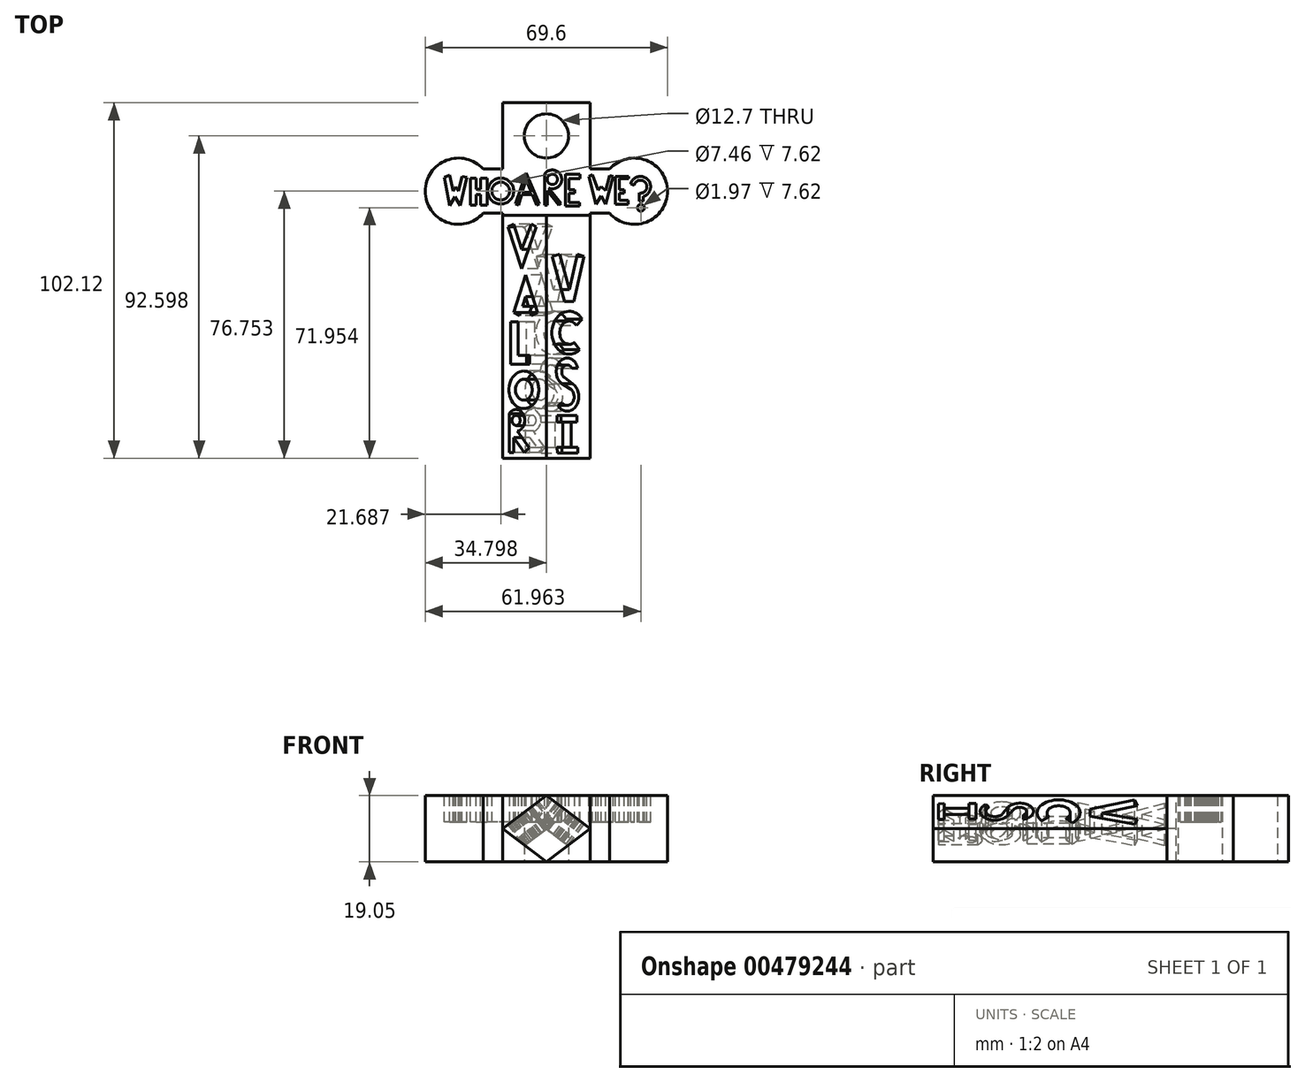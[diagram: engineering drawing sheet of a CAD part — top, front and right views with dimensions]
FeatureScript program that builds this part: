
annotation { "Feature Type Name" : "Feature", "Feature Type Description" : "" }
export const myFeature = defineFeature(function(context is Context, id is Id, definition is map)
    precondition{}
    {
        {
            var Q0;
            Q0=qCreatedBy(makeId("Top.planeOp"),FACE);
            var sketch = newSketch(context, id + "F0", { "sketchPlane" : qUnion([Q0])});
            skLineSegment(sketch, "E0", {"start": v(-32.4, 40.01) * mm, "end": v(-7.25, 40.01) * mm});
            skLineSegment(sketch, "E1", {"start": v(-32.4, 40.01) * mm, "end": v(-32.4, 20.96) * mm});
            skLineSegment(sketch, "E2", {"start": v(-7.25, 40.01) * mm, "end": v(-7.25, 20.96) * mm});
            skLineSegment(sketch, "E3", {"start": v(-7.25, 20.96) * mm, "end": v(5.45, 20.96) * mm});
            skLineSegment(sketch, "E4", {"start": v(-32.4, 20.96) * mm, "end": v(-45.1, 20.96) * mm});
            skLineSegment(sketch, "E5", {"start": v(-45.1, 8.26) * mm, "end": v(5.45, 8.26) * mm});
            skLineSegment(sketch, "E6", {"start": v(-32.4, 8.26) * mm, "end": v(-32.4, -45.49) * mm});
            skLineSegment(sketch, "E7", {"start": v(-7.25, 8.26) * mm, "end": v(-7.25, -45.49) * mm});
            skLineSegment(sketch, "E8", {"start": v(-19.82, 8.26) * mm, "end": v(-19.82, -62.1) * mm});
            skPoint(sketch, "E9.orphan", {"position": v(-7.25, -62.1) * mm});
            skPoint(sketch, "E10.orphan", {"position": v(-32.4, -62.1) * mm});
            skLineSegment(sketch, "E11", {"start": v(-32.4, 20.96) * mm, "end": v(-7.25, 20.96) * mm});
            skCircle(sketch, "E12", {"center": v(-19.82, 30.49) * mm, "radius": 6.35 * mm});
            skPoint(sketch, "E12.centerSnap0", {"position": v(-32.4, 30.49) * mm});
            skPoint(sketch, "E12.centerSnap1", {"position": v(-19.82, 40.01) * mm});
            skLineSegment(sketch, "E13", {"start": v(-7.25, -45.49) * mm, "end": v(-7.25, -62.1) * mm});
            skLineSegment(sketch, "E14", {"start": v(-32.4, -62.1) * mm, "end": v(-32.4, -45.49) * mm});
            skLineSegment(sketch, "E15", {"start": v(-7.25, -62.1) * mm, "end": v(-32.4, -62.1) * mm});
            skLineSegment(sketch, "E16", {"start": v(-19.82, 8.26) * mm, "end": v(-19.82, 20.96) * mm});
            skPoint(sketch, "E17.center.orphan", {"position": v(5.45, 14.61) * mm});
            skPoint(sketch, "E18.center.orphan", {"position": v(-45.1, 14.61) * mm});
            skArc(sketch, "E19", {"start": v(-38, 20.96) * mm, "mid": v(-54.62, 14.61) * mm, "end": v(-38, 8.26) * mm});
            skArc(sketch, "E20", {"start": v(-1.65, 8.26) * mm, "mid": v(14.98, 14.61) * mm, "end": v(-1.65, 20.96) * mm});
            skLineSegment(sketch, "E21", {"start": v(-45.1, 20.96) * mm, "end": v(-45.1, 8.26) * mm});
            skLineSegment(sketch, "E22", {"start": v(5.45, 20.96) * mm, "end": v(5.45, 8.26) * mm});
            skSolve(sketch);
        }
        {
            var Q0;
            Q0=makeQuery(id+"F0.imprint","IMPRINT",FACE,{"disambiguationData":[TD([[makeQuery(id+"F0.imprint","IMPRINT",EDGE,{"derivedFrom":sQuery(id+"F0.wireOp",EDGE,"E0")}),-1.0]])]});
            var Q1;
            {var subQ9=sQuery(id+"F0.wireOp",EDGE,"E16");Q1=makeQuery(id+"F0.imprint","IMPRINT",FACE,{"disambiguationData":[TD([[makeQuery(id+"F0.imprint","IMPRINT",EDGE,{"derivedFrom":subQ9}),1.0]])]});}
            var Q2;
            {var subQ4=sQuery(id+"F0.wireOp",EDGE,"E16");Q2=makeQuery(id+"F0.imprint","IMPRINT",FACE,{"disambiguationData":[TD([[makeQuery(id+"F0.imprint","IMPRINT",EDGE,{"derivedFrom":subQ4}),-1.0]])]});}
            var Q3;
            {var subQ2=sQuery(id+"F0.wireOp",EDGE,"E20");Q3=makeQuery(id+"F0.imprint","IMPRINT",FACE,{"disambiguationData":[TD([[makeQuery(id+"F0.imprint","IMPRINT",EDGE,{"derivedFrom":subQ2}),1.0]])]});}
            var Q4;
            {var subQ2=sQuery(id+"F0.wireOp",EDGE,"E19");Q4=makeQuery(id+"F0.imprint","IMPRINT",FACE,{"disambiguationData":[TD([[makeQuery(id+"F0.imprint","IMPRINT",EDGE,{"derivedFrom":subQ2}),1.0]])]});}
            var Q5;
            {var subQ1=sQuery(id+"F0.wireOp",EDGE,"E6");Q5=makeQuery(id+"F0.imprint","IMPRINT",FACE,{"disambiguationData":[TD([[makeQuery(id+"F0.imprint","IMPRINT",EDGE,{"derivedFrom":subQ1}),1.0]])]});}
            var Q6;
            {var subQ1=sQuery(id+"F0.wireOp",EDGE,"E7");Q6=makeQuery(id+"F0.imprint","IMPRINT",FACE,{"disambiguationData":[TD([[makeQuery(id+"F0.imprint","IMPRINT",EDGE,{"derivedFrom":subQ1}),-1.0]])]});}
            extrude(context, id + "F1", {"entities" : qUnion([Q0, Q1, Q2, Q3, Q4, Q5, Q6]), "depth" : 19.05 * mm});
        }
        {
            var Q0;
            Q0=makeQuery(id+"F1.opExtrude","SWEPT_FACE",FACE,{"disambiguationData":[OSD([sQuery(id+"F0.wireOp",EDGE,"E15")])]});
            var sketch = newSketch(context, id + "F2", { "sketchPlane" : qUnion([Q0])});
            skLineSegment(sketch, "E23", {"start": v(-19.82, 19.05) * mm, "end": v(-7.25, 9.53) * mm});
            skLineSegment(sketch, "E24", {"start": v(-7.25, 9.53) * mm, "end": v(-19.82, 0) * mm});
            skLineSegment(sketch, "E25", {"start": v(-19.82, 0) * mm, "end": v(-32.4, 9.53) * mm});
            skLineSegment(sketch, "E26", {"start": v(-32.4, 9.53) * mm, "end": v(-19.82, 19.05) * mm});
            skSolve(sketch);
        }
        {
            var Q0;
            {var subQ0=sQuery(id+"F2.wireOp",EDGE,"E23");Q0=makeQuery(id+"F2.imprint","IMPRINT",FACE,{"disambiguationData":[TD([[makeQuery(id+"F2.imprint","IMPRINT",EDGE,{"derivedFrom":subQ0}),1.0]])]});}
            var Q1;
            {var subQ0=sQuery(id+"F2.wireOp",EDGE,"E24");Q1=makeQuery(id+"F2.imprint","IMPRINT",FACE,{"disambiguationData":[TD([[makeQuery(id+"F2.imprint","IMPRINT",EDGE,{"derivedFrom":subQ0}),1.0]])]});}
            var Q2;
            {var subQ0=sQuery(id+"F2.wireOp",EDGE,"E25");Q2=makeQuery(id+"F2.imprint","IMPRINT",FACE,{"disambiguationData":[TD([[makeQuery(id+"F2.imprint","IMPRINT",EDGE,{"derivedFrom":subQ0}),1.0]])]});}
            var Q3;
            {var subQ0=sQuery(id+"F2.wireOp",EDGE,"E26");Q3=makeQuery(id+"F2.imprint","IMPRINT",FACE,{"disambiguationData":[TD([[makeQuery(id+"F2.imprint","IMPRINT",EDGE,{"derivedFrom":subQ0}),1.0]])]});}
            extrude(context, id + "F3", {"entities" : qUnion([Q0, Q1, Q2, Q3]), "operationType" : NewBodyOperationType.REMOVE, "oppositeDirection" : true, "depth" : 69.85 * mm});
        }
        {
            var Q0;
            Q0=makeQuery(id+"F3.boolean.opBoolean","COPY",FACE,{"derivedFrom":makeQuery(id+"F3.opExtrude","SWEPT_FACE",FACE,{"disambiguationData":[OSD([sQuery(id+"F2.wireOp",EDGE,"E23")])]})});
            var sketch = newSketch(context, id + "F4", { "sketchPlane" : qUnion([Q0])});
            skLineSegment(sketch, "E27", {"start": v(-27.3, 7.74) * mm, "end": v(-27.3, -62.1) * mm, "construction": true});
            skLineSegment(sketch, "E28", {"start": v(-25.2, -4.18) * mm, "end": v(-20.82, -17.04) * mm});
            skLineSegment(sketch, "E29", {"start": v(-20.82, -17.04) * mm, "end": v(-17.45, -17.04) * mm});
            skLineSegment(sketch, "E30", {"start": v(-17.45, -17.04) * mm, "end": v(-13.74, -4.18) * mm});
            skLineSegment(sketch, "E31", {"start": v(-13.74, -4.18) * mm, "end": v(-16.07, -3.5) * mm});
            skLineSegment(sketch, "E32", {"start": v(-16.07, -3.5) * mm, "end": v(-19, -13.62) * mm});
            skLineSegment(sketch, "E33", {"start": v(-19, -13.62) * mm, "end": v(-22.44, -3.5) * mm});
            skLineSegment(sketch, "E34", {"start": v(-22.44, -3.5) * mm, "end": v(-25.2, -4.18) * mm});
            skArc(sketch, "E35", {"start": v(-14.32, -22.2) * mm, "mid": v(-25.28, -25.38) * mm, "end": v(-15.3, -30.91) * mm});
            skArc(sketch, "E36", {"start": v(-16.51, -23.97) * mm, "mid": v(-22.45, -25.54) * mm, "end": v(-17.3, -28.88) * mm});
            skLineSegment(sketch, "E37", {"start": v(-16.51, -23.97) * mm, "end": v(-14.32, -22.2) * mm});
            skLineSegment(sketch, "E38", {"start": v(-17.3, -28.88) * mm, "end": v(-15.3, -30.91) * mm});
            skArc(sketch, "E39", {"start": v(-16, -36.26) * mm, "mid": v(-22.36, -34.27) * mm, "end": v(-21.4, -40.86) * mm});
            skArc(sketch, "E40", {"start": v(-18.13, -36.26) * mm, "mid": v(-21.18, -35.87) * mm, "end": v(-20.84, -38.93) * mm});
            skLineSegment(sketch, "E41", {"start": v(-18.13, -36.26) * mm, "end": v(-16, -36.26) * mm});
            skPoint(sketch, "E42.center.orphan", {"position": v(-19.8, -45.95) * mm});
            skArc(sketch, "E43", {"start": v(-23.1, -47.02) * mm, "mid": v(-16.58, -47.1) * mm, "end": v(-17.93, -40.72) * mm});
            skArc(sketch, "E44", {"start": v(-21.68, -46.13) * mm, "mid": v(-17.8, -45.97) * mm, "end": v(-18.7, -42.2) * mm});
            skLineSegment(sketch, "E45", {"start": v(-23.1, -47.02) * mm, "end": v(-21.68, -46.13) * mm});
            skLineSegment(sketch, "E46", {"start": v(-21.69, -40.72) * mm, "end": v(-17.51, -42.78) * mm});
            skPoint(sketch, "E47.end.orphan", {"position": v(-21.69, -42.78) * mm});
            skLineSegment(sketch, "E48", {"start": v(-17.93, -40.72) * mm, "end": v(-20.84, -38.93) * mm});
            skLineSegment(sketch, "E49", {"start": v(-21.33, -51.8) * mm, "end": v(-21.33, -58.99) * mm});
            skLineSegment(sketch, "E50", {"start": v(-21.33, -58.99) * mm, "end": v(-23.52, -58.99) * mm});
            skLineSegment(sketch, "E51", {"start": v(-23.52, -58.99) * mm, "end": v(-23.35, -60.66) * mm});
            skLineSegment(sketch, "E52", {"start": v(-23.35, -60.66) * mm, "end": v(-15.93, -60.66) * mm});
            skLineSegment(sketch, "E53", {"start": v(-15.93, -60.66) * mm, "end": v(-15.92, -58.99) * mm});
            skLineSegment(sketch, "E54", {"start": v(-15.92, -58.99) * mm, "end": v(-18.3, -58.98) * mm});
            skLineSegment(sketch, "E55", {"start": v(-18.3, -58.98) * mm, "end": v(-18.3, -51.8) * mm});
            skLineSegment(sketch, "E56", {"start": v(-18.3, -51.8) * mm, "end": v(-16.27, -51.8) * mm});
            skLineSegment(sketch, "E57", {"start": v(-16.27, -51.8) * mm, "end": v(-16.27, -49.8) * mm});
            skLineSegment(sketch, "E58", {"start": v(-16.27, -49.8) * mm, "end": v(-23.52, -49.8) * mm});
            skLineSegment(sketch, "E59", {"start": v(-23.52, -49.8) * mm, "end": v(-23.52, -51.8) * mm});
            skLineSegment(sketch, "E60", {"start": v(-23.52, -51.8) * mm, "end": v(-21.33, -51.8) * mm});
            skLineSegment(sketch, "E61.MirrorCS", {"start": v(-32.17, -3.5) * mm, "end": v(-29.4, -4.18) * mm});
            skLineSegment(sketch, "E62.MirrorCS", {"start": v(-29.4, -4.18) * mm, "end": v(-33.79, -17.04) * mm});
            skLineSegment(sketch, "E63.MirrorCS", {"start": v(-35.62, -13.62) * mm, "end": v(-32.17, -3.5) * mm});
            skLineSegment(sketch, "E64.MirrorCS", {"start": v(-38.54, -3.5) * mm, "end": v(-35.62, -13.62) * mm});
            skLineSegment(sketch, "E65.MirrorCS", {"start": v(-40.87, -4.18) * mm, "end": v(-38.54, -3.5) * mm});
            skLineSegment(sketch, "E66.MirrorCS", {"start": v(-37.16, -17.04) * mm, "end": v(-40.87, -4.18) * mm});
            skLineSegment(sketch, "E67.MirrorCS", {"start": v(-33.79, -17.04) * mm, "end": v(-37.16, -17.04) * mm});
            skArc(sketch, "E68.MirrorCS", {"start": v(-40.29, -22.2) * mm, "mid": v(-29.33, -25.38) * mm, "end": v(-39.31, -30.91) * mm});
            skLineSegment(sketch, "E69.MirrorCS", {"start": v(-37.3, -28.88) * mm, "end": v(-39.31, -30.91) * mm});
            skArc(sketch, "E70.MirrorCS", {"start": v(-38.1, -23.97) * mm, "mid": v(-32.16, -25.54) * mm, "end": v(-37.3, -28.88) * mm});
            skLineSegment(sketch, "E71.MirrorCS", {"start": v(-38.1, -23.97) * mm, "end": v(-40.29, -22.2) * mm});
            skArc(sketch, "E72.MirrorCS", {"start": v(-38.6, -36.26) * mm, "mid": v(-32.25, -34.27) * mm, "end": v(-33.2, -40.86) * mm});
            skArc(sketch, "E73.MirrorCS", {"start": v(-36.48, -36.26) * mm, "mid": v(-33.43, -35.87) * mm, "end": v(-33.77, -38.93) * mm});
            skLineSegment(sketch, "E74.MirrorCS", {"start": v(-36.68, -40.72) * mm, "end": v(-33.77, -38.93) * mm});
            skArc(sketch, "E75.MirrorCS", {"start": v(-31.51, -47.02) * mm, "mid": v(-38.03, -47.1) * mm, "end": v(-36.68, -40.72) * mm});
            skPoint(sketch, "E76.MirrorP", {"position": v(-34.8, -45.95) * mm});
            skArc(sketch, "E77.MirrorCS", {"start": v(-32.92, -46.13) * mm, "mid": v(-36.8, -45.97) * mm, "end": v(-35.9, -42.2) * mm});
            skLineSegment(sketch, "E78.MirrorCS", {"start": v(-32.92, -40.72) * mm, "end": v(-37.1, -42.78) * mm});
            skLineSegment(sketch, "E79.MirrorCS", {"start": v(-36.48, -36.26) * mm, "end": v(-38.6, -36.26) * mm});
            skLineSegment(sketch, "E80.MirrorCS", {"start": v(-31.51, -47.02) * mm, "end": v(-32.92, -46.13) * mm});
            skLineSegment(sketch, "E81.MirrorCS", {"start": v(-38.34, -49.8) * mm, "end": v(-31.09, -49.8) * mm});
            skLineSegment(sketch, "E82.MirrorCS", {"start": v(-36.32, -51.8) * mm, "end": v(-38.34, -51.8) * mm});
            skLineSegment(sketch, "E83.MirrorCS", {"start": v(-38.34, -51.8) * mm, "end": v(-38.34, -49.8) * mm});
            skLineSegment(sketch, "E84.MirrorCS", {"start": v(-31.09, -49.8) * mm, "end": v(-31.09, -51.8) * mm});
            skLineSegment(sketch, "E85.MirrorCS", {"start": v(-31.09, -51.8) * mm, "end": v(-33.28, -51.8) * mm});
            skLineSegment(sketch, "E86.MirrorCS", {"start": v(-33.28, -51.8) * mm, "end": v(-33.28, -58.99) * mm});
            skLineSegment(sketch, "E87.MirrorCS", {"start": v(-36.32, -58.98) * mm, "end": v(-36.32, -51.8) * mm});
            skLineSegment(sketch, "E88.MirrorCS", {"start": v(-31.26, -60.66) * mm, "end": v(-38.68, -60.66) * mm});
            skLineSegment(sketch, "E89.MirrorCS", {"start": v(-38.68, -58.99) * mm, "end": v(-36.32, -58.98) * mm});
            skLineSegment(sketch, "E90.MirrorCS", {"start": v(-31.09, -58.99) * mm, "end": v(-31.26, -60.66) * mm});
            skLineSegment(sketch, "E91.MirrorCS", {"start": v(-38.68, -60.66) * mm, "end": v(-38.68, -58.99) * mm});
            skLineSegment(sketch, "E92", {"start": v(-31.09, -58.99) * mm, "end": v(-33.28, -58.99) * mm});
            skSolve(sketch);
        }
        {
            var Q0;
            Q0=makeQuery(id+"F4.imprint","IMPRINT",FACE,{"disambiguationData":[TD([[makeQuery(id+"F4.imprint","IMPRINT",EDGE,{"derivedFrom":sQuery(id+"F4.wireOp",EDGE,"E28")}),1.0]])]});
            var Q1;
            Q1=makeQuery(id+"F4.imprint","IMPRINT",FACE,{"disambiguationData":[TD([[makeQuery(id+"F4.imprint","IMPRINT",EDGE,{"derivedFrom":sQuery(id+"F4.wireOp",EDGE,"E35")}),1.0]])]});
            var Q2;
            Q2=makeQuery(id+"F4.imprint","IMPRINT",FACE,{"disambiguationData":[TD([[makeQuery(id+"F4.imprint","IMPRINT",EDGE,{"derivedFrom":sQuery(id+"F4.wireOp",EDGE,"E40")}),-1.0]])]});
            var Q3;
            Q3=makeQuery(id+"F4.imprint","IMPRINT",FACE,{"disambiguationData":[TD([[makeQuery(id+"F4.imprint","IMPRINT",EDGE,{"derivedFrom":sQuery(id+"F4.wireOp",EDGE,"E49")}),1.0]])]});
            extrude(context, id + "F5", {"entities" : qUnion([Q0, Q1, Q2, Q3]), "operationType" : NewBodyOperationType.REMOVE, "oppositeDirection" : true, "depth" : 7.62 * mm});
        }
        {
            var Q0;
            Q0=makeQuery(id+"F1.opExtrude","CAP_FACE",FACE,{"disambiguationData":[OSD([sQuery(id+"F0.wireOp",EDGE,"E0"),sQuery(id+"F0.wireOp",EDGE,"E1"),sQuery(id+"F0.wireOp",EDGE,"E2"),sQuery(id+"F0.wireOp",EDGE,"E3"),sQuery(id+"F0.wireOp",EDGE,"E4"),sQuery(id+"F0.wireOp",EDGE,"E5"),sQuery(id+"F0.wireOp",EDGE,"E6"),sQuery(id+"F0.wireOp",EDGE,"E7"),sQuery(id+"F0.wireOp",EDGE,"E12"),sQuery(id+"F0.wireOp",EDGE,"E13"),sQuery(id+"F0.wireOp",EDGE,"E14"),sQuery(id+"F0.wireOp",EDGE,"E15"),sQuery(id+"F0.wireOp",EDGE,"E19"),sQuery(id+"F0.wireOp",EDGE,"E20")])],"isStart":false});
            var sketch = newSketch(context, id + "F6", { "sketchPlane" : qUnion([Q0])});
            skLineSegment(sketch, "E93", {"start": v(-49.1, 18.55) * mm, "end": v(-47.63, 10.47) * mm});
            skLineSegment(sketch, "E94", {"start": v(-47.63, 10.47) * mm, "end": v(-46.06, 13.07) * mm});
            skLineSegment(sketch, "E95", {"start": v(-46.06, 13.07) * mm, "end": v(-44.59, 10.47) * mm});
            skLineSegment(sketch, "E96", {"start": v(-44.59, 10.47) * mm, "end": v(-42.67, 18.55) * mm});
            skLineSegment(sketch, "E97", {"start": v(-42.67, 18.55) * mm, "end": v(-44.05, 18.87) * mm});
            skLineSegment(sketch, "E98", {"start": v(-44.05, 18.87) * mm, "end": v(-45.1, 14.61) * mm});
            skLineSegment(sketch, "E99", {"start": v(-45.1, 14.61) * mm, "end": v(-45.8, 15.77) * mm});
            skLineSegment(sketch, "E100", {"start": v(-45.8, 15.77) * mm, "end": v(-46.58, 14.61) * mm});
            skLineSegment(sketch, "E101", {"start": v(-46.58, 14.61) * mm, "end": v(-47.63, 19.24) * mm});
            skLineSegment(sketch, "E102", {"start": v(-47.63, 19.24) * mm, "end": v(-49.1, 18.55) * mm});
            skLineSegment(sketch, "E103", {"start": v(-41.72, 18.37) * mm, "end": v(-41.72, 10.55) * mm});
            skLineSegment(sketch, "E104", {"start": v(-41.72, 10.55) * mm, "end": v(-40.07, 10.55) * mm});
            skLineSegment(sketch, "E105", {"start": v(-40.07, 10.55) * mm, "end": v(-40.07, 13.6) * mm});
            skLineSegment(sketch, "E106", {"start": v(-40.07, 13.6) * mm, "end": v(-38.68, 13.6) * mm});
            skLineSegment(sketch, "E107", {"start": v(-38.68, 13.6) * mm, "end": v(-38.68, 10.55) * mm});
            skLineSegment(sketch, "E108", {"start": v(-38.68, 10.55) * mm, "end": v(-36.85, 10.55) * mm});
            skLineSegment(sketch, "E109", {"start": v(-36.85, 10.55) * mm, "end": v(-36.85, 18.37) * mm});
            skLineSegment(sketch, "E110", {"start": v(-36.85, 18.37) * mm, "end": v(-38.68, 18.37) * mm});
            skLineSegment(sketch, "E111", {"start": v(-38.68, 18.37) * mm, "end": v(-38.68, 15.16) * mm});
            skLineSegment(sketch, "E112", {"start": v(-38.68, 15.16) * mm, "end": v(-40.07, 15.16) * mm});
            skLineSegment(sketch, "E113", {"start": v(-40.07, 15.16) * mm, "end": v(-40.07, 18.37) * mm});
            skLineSegment(sketch, "E114", {"start": v(-40.07, 18.37) * mm, "end": v(-41.72, 18.37) * mm});
            skCircle(sketch, "E115", {"center": v(-32.93, 14.64) * mm, "radius": 3.73 * mm});
            skCircle(sketch, "E116", {"center": v(-32.93, 14.64) * mm, "radius": 2.56 * mm});
            skLineSegment(sketch, "E117", {"start": v(-27.85, 10.64) * mm, "end": v(-26.95, 13.66) * mm});
            skLineSegment(sketch, "E118", {"start": v(-25.68, 17.95) * mm, "end": v(-24.12, 14.3) * mm});
            skLineSegment(sketch, "E119", {"start": v(-22.57, 10.64) * mm, "end": v(-21.87, 10.93) * mm});
            skLineSegment(sketch, "E120", {"start": v(-21.87, 10.93) * mm, "end": v(-25.68, 19.87) * mm});
            skLineSegment(sketch, "E121", {"start": v(-25.68, 19.87) * mm, "end": v(-28.67, 10.93) * mm});
            skLineSegment(sketch, "E122", {"start": v(-28.67, 10.93) * mm, "end": v(-27.85, 10.64) * mm});
            skLineSegment(sketch, "E123", {"start": v(-26.76, 14.3) * mm, "end": v(-24.12, 14.3) * mm});
            skLineSegment(sketch, "E124", {"start": v(-26.95, 13.66) * mm, "end": v(-23.86, 13.66) * mm});
            skLineSegment(sketch, "E125.trimOffspring", {"start": v(-26.76, 14.3) * mm, "end": v(-25.68, 17.95) * mm});
            skLineSegment(sketch, "E126.trimOffspring", {"start": v(-23.86, 13.66) * mm, "end": v(-22.57, 10.64) * mm});
            skLineSegment(sketch, "E127", {"start": v(-20.28, 19.67) * mm, "end": v(-20.28, 10.64) * mm});
            skLineSegment(sketch, "E128", {"start": v(-20.28, 10.64) * mm, "end": v(-19.58, 10.62) * mm});
            skLineSegment(sketch, "E129", {"start": v(-19.58, 10.62) * mm, "end": v(-19.58, 14.83) * mm});
            skLineSegment(sketch, "E130", {"start": v(-19.58, 14.83) * mm, "end": v(-16.2, 10.62) * mm});
            skLineSegment(sketch, "E131", {"start": v(-16.2, 10.62) * mm, "end": v(-15.64, 11.07) * mm});
            skLineSegment(sketch, "E132", {"start": v(-15.64, 11.07) * mm, "end": v(-19.3, 15.65) * mm});
            skArc(sketch, "E133", {"start": v(-19.2, 15.52) * mm, "mid": v(-15.49, 18.7) * mm, "end": v(-20.28, 19.66) * mm});
            skCircle(sketch, "E134", {"center": v(-18.11, 18.01) * mm, "radius": 1.48 * mm});
            skLineSegment(sketch, "E135", {"start": v(-14.36, 18.2) * mm, "end": v(-14.36, 10.32) * mm});
            skLineSegment(sketch, "E136", {"start": v(-14.49, 10.32) * mm, "end": v(-10.3, 10.32) * mm});
            skLineSegment(sketch, "E137", {"start": v(-10.3, 10.32) * mm, "end": v(-10.3, 11.4) * mm});
            skLineSegment(sketch, "E138", {"start": v(-10.3, 11.4) * mm, "end": v(-13.28, 11.4) * mm});
            skLineSegment(sketch, "E139", {"start": v(-13.28, 11.4) * mm, "end": v(-13.28, 14) * mm});
            skLineSegment(sketch, "E140", {"start": v(-13.28, 14) * mm, "end": v(-11.63, 14) * mm});
            skLineSegment(sketch, "E141", {"start": v(-11.63, 14) * mm, "end": v(-11.63, 15.09) * mm});
            skLineSegment(sketch, "E142", {"start": v(-11.63, 15.09) * mm, "end": v(-13.28, 15.09) * mm});
            skLineSegment(sketch, "E143", {"start": v(-13.28, 15.09) * mm, "end": v(-13.28, 18.27) * mm});
            skLineSegment(sketch, "E144", {"start": v(-13.28, 18.27) * mm, "end": v(-10.16, 18.27) * mm});
            skLineSegment(sketch, "E145", {"start": v(-10.16, 18.27) * mm, "end": v(-10.16, 19.48) * mm});
            skLineSegment(sketch, "E146", {"start": v(-10.16, 19.48) * mm, "end": v(-14.36, 19.48) * mm});
            skLineSegment(sketch, "E147", {"start": v(-14.36, 19.48) * mm, "end": v(-14.36, 18.2) * mm});
            skLineSegment(sketch, "E148", {"start": v(-7.62, 18.84) * mm, "end": v(-5.59, 10.83) * mm});
            skLineSegment(sketch, "E149", {"start": v(-5.59, 10.83) * mm, "end": v(-4.06, 13.3) * mm});
            skLineSegment(sketch, "E150", {"start": v(-4.06, 13.3) * mm, "end": v(-2.85, 10.83) * mm});
            skLineSegment(sketch, "E151", {"start": v(-2.85, 10.83) * mm, "end": v(-0.69, 18.84) * mm});
            skLineSegment(sketch, "E152", {"start": v(-0.69, 18.84) * mm, "end": v(-1.68, 19.1) * mm});
            skLineSegment(sketch, "E153", {"start": v(-1.68, 19.1) * mm, "end": v(-2.85, 14.78) * mm});
            skLineSegment(sketch, "E154", {"start": v(-2.85, 14.78) * mm, "end": v(-4.06, 15.91) * mm});
            skLineSegment(sketch, "E155", {"start": v(-4.06, 15.91) * mm, "end": v(-5.01, 14.9) * mm});
            skLineSegment(sketch, "E156", {"start": v(-5.01, 14.9) * mm, "end": v(-6.6, 19.41) * mm});
            skLineSegment(sketch, "E157", {"start": v(-6.6, 19.41) * mm, "end": v(-7.62, 18.84) * mm});
            skLineSegment(sketch, "E158", {"start": v(0, 18.84) * mm, "end": v(0, 10.83) * mm});
            skLineSegment(sketch, "E159", {"start": v(0, 10.83) * mm, "end": v(3.7, 10.83) * mm});
            skLineSegment(sketch, "E160", {"start": v(3.7, 10.83) * mm, "end": v(3.7, 12.04) * mm});
            skLineSegment(sketch, "E161", {"start": v(3.7, 12.04) * mm, "end": v(1.16, 12.04) * mm});
            skLineSegment(sketch, "E162", {"start": v(1.16, 12.04) * mm, "end": v(1.16, 14) * mm});
            skLineSegment(sketch, "E163", {"start": v(1.16, 14) * mm, "end": v(2.56, 14) * mm});
            skLineSegment(sketch, "E164", {"start": v(2.56, 14) * mm, "end": v(2.56, 15.02) * mm});
            skLineSegment(sketch, "E165", {"start": v(2.56, 15.02) * mm, "end": v(1.1, 15.02) * mm});
            skLineSegment(sketch, "E166", {"start": v(1.1, 15.02) * mm, "end": v(1.1, 18.2) * mm});
            skLineSegment(sketch, "E167", {"start": v(1.1, 18.2) * mm, "end": v(3.76, 18.2) * mm});
            skLineSegment(sketch, "E168", {"start": v(3.76, 18.2) * mm, "end": v(3.76, 18.84) * mm});
            skLineSegment(sketch, "E169", {"start": v(3.76, 18.84) * mm, "end": v(0, 18.84) * mm});
            skArc(sketch, "E170", {"start": v(8.02, 13.11) * mm, "mid": v(9.3, 18) * mm, "end": v(4.4, 16.74) * mm});
            skArc(sketch, "E171", {"start": v(6.86, 14.11) * mm, "mid": v(8.78, 16.92) * mm, "end": v(5.42, 16.36) * mm});
            skLineSegment(sketch, "E172", {"start": v(4.4, 16.74) * mm, "end": v(5.42, 16.36) * mm});
            skLineSegment(sketch, "E173", {"start": v(6.86, 14.11) * mm, "end": v(6.86, 11.69) * mm});
            skLineSegment(sketch, "E174", {"start": v(8.02, 13.11) * mm, "end": v(8.02, 11.69) * mm});
            skLineSegment(sketch, "E175", {"start": v(8.02, 11.69) * mm, "end": v(6.86, 11.69) * mm});
            skCircle(sketch, "E176", {"center": v(7.34, 9.84) * mm, "radius": 0.98 * mm});
            skSolve(sketch);
        }
        {
            var Q0;
            Q0=makeQuery(id+"F6.imprint","IMPRINT",FACE,{"disambiguationData":[TD([[makeQuery(id+"F6.imprint","IMPRINT",EDGE,{"derivedFrom":sQuery(id+"F6.wireOp",EDGE,"E93")}),1.0]])]});
            var Q1;
            Q1=makeQuery(id+"F6.imprint","IMPRINT",FACE,{"disambiguationData":[TD([[makeQuery(id+"F6.imprint","IMPRINT",EDGE,{"derivedFrom":sQuery(id+"F6.wireOp",EDGE,"E103")}),1.0]])]});
            var Q2;
            Q2=makeQuery(id+"F6.imprint","IMPRINT",FACE,{"disambiguationData":[TD([[makeQuery(id+"F6.imprint","IMPRINT",EDGE,{"derivedFrom":sQuery(id+"F6.wireOp",EDGE,"E115")}),1.0]])]});
            var Q3;
            Q3=makeQuery(id+"F6.imprint","IMPRINT",FACE,{"disambiguationData":[TD([[makeQuery(id+"F6.imprint","IMPRINT",EDGE,{"derivedFrom":sQuery(id+"F6.wireOp",EDGE,"E117")}),1.0]])]});
            var Q4;
            {var subQ0=sQuery(id+"F6.wireOp",EDGE,"E128");Q4=makeQuery(id+"F6.imprint","IMPRINT",FACE,{"disambiguationData":[TD([[makeQuery(id+"F6.imprint","IMPRINT",EDGE,{"derivedFrom":subQ0}),1.0]])]});}
            var Q5;
            {var subQ0=sQuery(id+"F6.wireOp",EDGE,"E135");Q5=makeQuery(id+"F6.imprint","IMPRINT",FACE,{"disambiguationData":[TD([[makeQuery(id+"F6.imprint","IMPRINT",EDGE,{"derivedFrom":subQ0}),1.0]])]});}
            var Q6;
            Q6=makeQuery(id+"F6.imprint","IMPRINT",FACE,{"disambiguationData":[TD([[makeQuery(id+"F6.imprint","IMPRINT",EDGE,{"derivedFrom":sQuery(id+"F6.wireOp",EDGE,"E148")}),1.0]])]});
            var Q7;
            Q7=makeQuery(id+"F6.imprint","IMPRINT",FACE,{"disambiguationData":[TD([[makeQuery(id+"F6.imprint","IMPRINT",EDGE,{"derivedFrom":sQuery(id+"F6.wireOp",EDGE,"E158")}),1.0]])]});
            var Q8;
            Q8=makeQuery(id+"F6.imprint","IMPRINT",FACE,{"disambiguationData":[TD([[makeQuery(id+"F6.imprint","IMPRINT",EDGE,{"derivedFrom":sQuery(id+"F6.wireOp",EDGE,"E170")}),1.0]])]});
            var Q9;
            Q9=makeQuery(id+"F6.imprint","IMPRINT",FACE,{"disambiguationData":[TD([[makeQuery(id+"F6.imprint","IMPRINT",EDGE,{"derivedFrom":sQuery(id+"F6.wireOp",EDGE,"E176")}),1.0]])]});
            extrude(context, id + "F7", {"entities" : qUnion([Q0, Q1, Q2, Q3, Q4, Q5, Q6, Q7, Q8, Q9]), "operationType" : NewBodyOperationType.REMOVE, "oppositeDirection" : true, "depth" : 7.62 * mm});
        }
        {
            var Q0;
            Q0=makeQuery(id+"F3.boolean.opBoolean","COPY",FACE,{"derivedFrom":makeQuery(id+"F3.opExtrude","SWEPT_FACE",FACE,{"disambiguationData":[OSD([sQuery(id+"F2.wireOp",EDGE,"E26")])]})});
            var sketch = newSketch(context, id + "F8", { "sketchPlane" : qUnion([Q0])});
            skLineSegment(sketch, "E177", {"start": v(-18.06, 4.36) * mm, "end": v(-13.2, -7.67) * mm});
            skLineSegment(sketch, "E178", {"start": v(-13.2, -7.67) * mm, "end": v(-7.9, 4.36) * mm});
            skLineSegment(sketch, "E179", {"start": v(-7.9, 4.36) * mm, "end": v(-9.66, 5.14) * mm});
            skLineSegment(sketch, "E180", {"start": v(-18.06, 4.36) * mm, "end": v(-16.13, 5.14) * mm});
            skLineSegment(sketch, "E181", {"start": v(-16.13, 5.14) * mm, "end": v(-13.2, -2.1) * mm});
            skLineSegment(sketch, "E182", {"start": v(-13.2, -2.1) * mm, "end": v(-9.66, 5.14) * mm});
            skLineSegment(sketch, "E183", {"start": v(-11.84, -9.47) * mm, "end": v(-16.13, -20.3) * mm});
            skLineSegment(sketch, "E184", {"start": v(-16.13, -20.3) * mm, "end": v(-13.98, -21.15) * mm});
            skPoint(sketch, "E184.endSnap0", {"position": v(-13.98, -14.89) * mm});
            skLineSegment(sketch, "E185", {"start": v(-13.98, -21.15) * mm, "end": v(-13.65, -20.3) * mm});
            skLineSegment(sketch, "E186", {"start": v(-11.84, -15.74) * mm, "end": v(-10.75, -18.45) * mm});
            skLineSegment(sketch, "E187", {"start": v(-9.65, -21.15) * mm, "end": v(-7.53, -20.3) * mm});
            skLineSegment(sketch, "E188", {"start": v(-7.53, -20.3) * mm, "end": v(-11.84, -9.47) * mm});
            skLineSegment(sketch, "E189", {"start": v(-10.75, -18.45) * mm, "end": v(-12.91, -18.45) * mm});
            skLineSegment(sketch, "E190", {"start": v(-13.98, -20.3) * mm, "end": v(-9.65, -20.3) * mm});
            skLineSegment(sketch, "E191.trimOffspring", {"start": v(-12.91, -18.45) * mm, "end": v(-11.84, -15.74) * mm});
            skLineSegment(sketch, "E192.trimOffspring", {"start": v(-10, -20.3) * mm, "end": v(-9.65, -21.15) * mm});
            skLineSegment(sketch, "E193", {"start": v(-17.19, -22.91) * mm, "end": v(-14.4, -22.91) * mm});
            skLineSegment(sketch, "E194", {"start": v(-14.4, -22.91) * mm, "end": v(-14.4, -32.52) * mm});
            skLineSegment(sketch, "E195", {"start": v(-14.4, -32.52) * mm, "end": v(-10.29, -32.52) * mm});
            skLineSegment(sketch, "E196", {"start": v(-10.29, -32.52) * mm, "end": v(-10.29, -35.13) * mm});
            skLineSegment(sketch, "E197", {"start": v(-10.29, -35.13) * mm, "end": v(-17.19, -35.13) * mm});
            skLineSegment(sketch, "E198", {"start": v(-17.19, -35.13) * mm, "end": v(-17.19, -22.91) * mm});
            skCircle(sketch, "E199", {"center": v(-12.42, -42.45) * mm, "radius": 5.38 * mm});
            skCircle(sketch, "E200", {"center": v(-12.42, -42.45) * mm, "radius": 3 * mm});
            skLineSegment(sketch, "E201", {"start": v(-17.68, -48.97) * mm, "end": v(-17.68, -60.53) * mm});
            skLineSegment(sketch, "E202", {"start": v(-17.68, -60.53) * mm, "end": v(-16.04, -60.53) * mm});
            skLineSegment(sketch, "E203", {"start": v(-16.04, -60.53) * mm, "end": v(-16.04, -56.13) * mm});
            skLineSegment(sketch, "E204", {"start": v(-16.04, -56.13) * mm, "end": v(-12.18, -60.53) * mm});
            skPoint(sketch, "E204.endSnap0", {"position": v(-12.18, -62.1) * mm});
            skLineSegment(sketch, "E205", {"start": v(-12.18, -60.53) * mm, "end": v(-10.56, -59.1) * mm});
            skLineSegment(sketch, "E206", {"start": v(-10.56, -59.1) * mm, "end": v(-14.83, -54.23) * mm});
            skArc(sketch, "E207", {"start": v(-14.74, -54.34) * mm, "mid": v(-12.52, -49.66) * mm, "end": v(-17.68, -49.32) * mm});
            skCircle(sketch, "E208", {"center": v(-15.22, -51.25) * mm, "radius": 1.47 * mm});
            skSolve(sketch);
        }
        {
            var Q0;
            Q0=makeQuery(id+"F8.imprint","IMPRINT",FACE,{"disambiguationData":[TD([[makeQuery(id+"F8.imprint","IMPRINT",EDGE,{"derivedFrom":sQuery(id+"F8.wireOp",EDGE,"E177")}),1.0]])]});
            var Q1;
            Q1=makeQuery(id+"F8.imprint","IMPRINT",FACE,{"disambiguationData":[TD([[makeQuery(id+"F8.imprint","IMPRINT",EDGE,{"derivedFrom":sQuery(id+"F8.wireOp",EDGE,"E183")}),1.0]])]});
            var Q2;
            Q2=makeQuery(id+"F8.imprint","IMPRINT",FACE,{"disambiguationData":[TD([[makeQuery(id+"F8.imprint","IMPRINT",EDGE,{"derivedFrom":sQuery(id+"F8.wireOp",EDGE,"E193")}),-1.0]])]});
            var Q3;
            Q3=makeQuery(id+"F8.imprint","IMPRINT",FACE,{"disambiguationData":[TD([[makeQuery(id+"F8.imprint","IMPRINT",EDGE,{"derivedFrom":sQuery(id+"F8.wireOp",EDGE,"E199")}),1.0]])]});
            var Q4;
            {var subQ0=sQuery(id+"F8.wireOp",EDGE,"E202");Q4=makeQuery(id+"F8.imprint","IMPRINT",FACE,{"disambiguationData":[TD([[makeQuery(id+"F8.imprint","IMPRINT",EDGE,{"derivedFrom":subQ0}),1.0]])]});}
            extrude(context, id + "F9", {"entities" : qUnion([Q0, Q1, Q2, Q3, Q4]), "operationType" : NewBodyOperationType.REMOVE, "oppositeDirection" : true, "depth" : 7.62 * mm});
        }
    });
